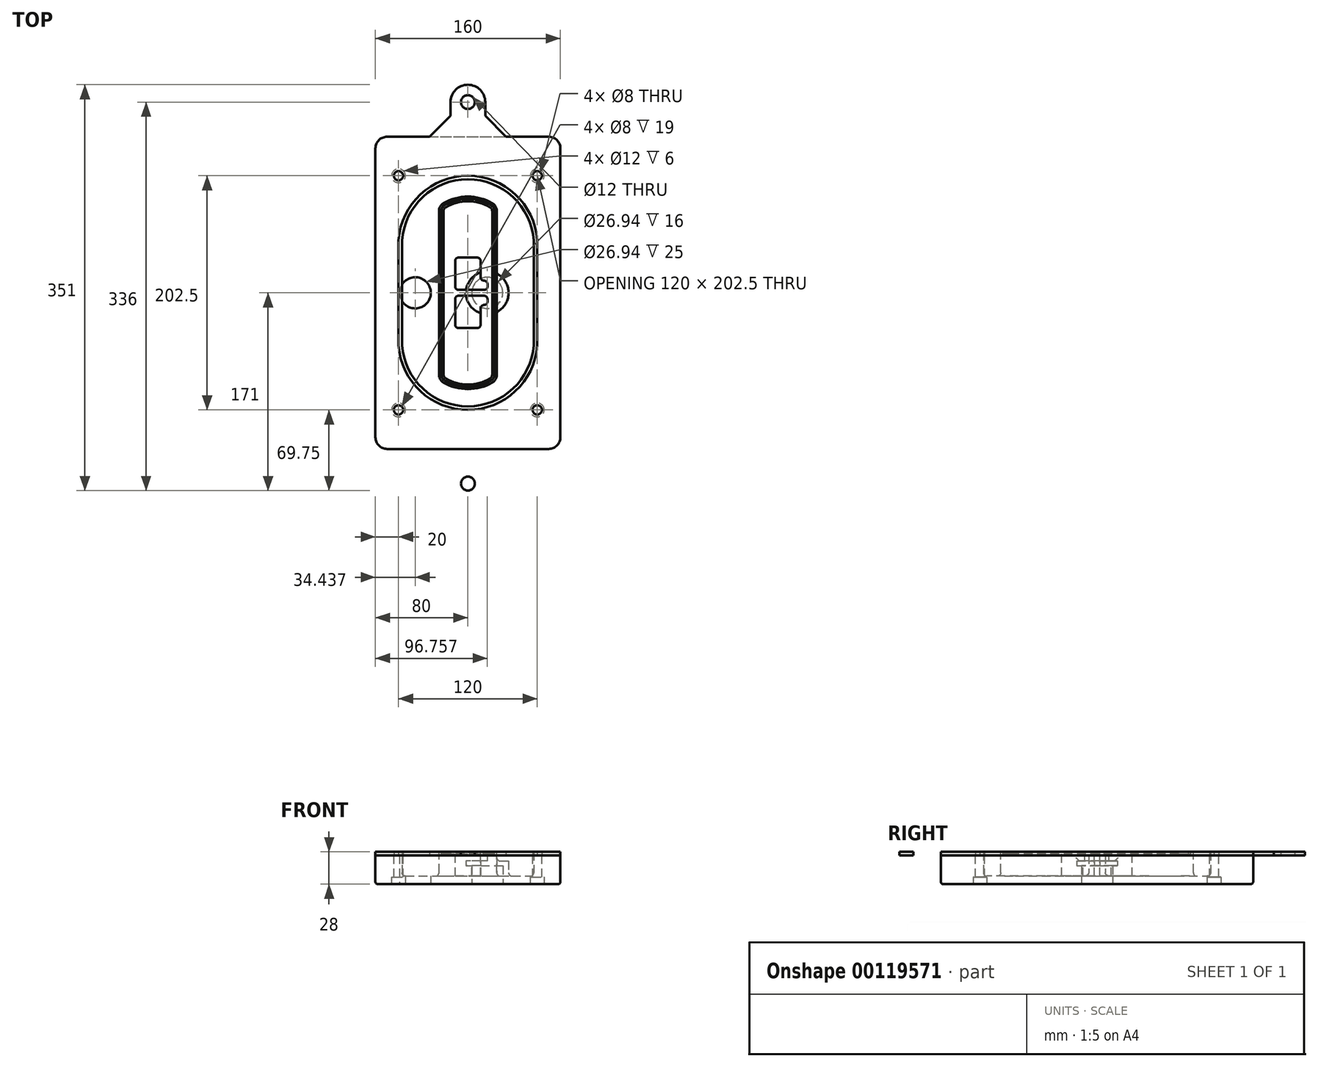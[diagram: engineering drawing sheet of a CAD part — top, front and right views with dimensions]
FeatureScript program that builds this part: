
annotation { "Feature Type Name" : "Feature", "Feature Type Description" : "" }
export const myFeature = defineFeature(function(context is Context, id is Id, definition is map)
    precondition{}
    {
        {
            var Q0;
            Q0=qCreatedBy(makeId("Top.planeOp"),FACE);
            var sketch = newSketch(context, id + "F0", { "sketchPlane" : qUnion([Q0])});
            skPoint(sketch, "E0.rect.middle", {"position": v(0, 0) * mm});
            skLineSegment(sketch, "E1.bottom", {"start": v(-70, -135) * mm, "end": v(70, -135) * mm});
            skLineSegment(sketch, "E1.top", {"start": v(-70, 135) * mm, "end": v(70, 135) * mm});
            skLineSegment(sketch, "E1.left", {"start": v(-80, -125) * mm, "end": v(-80, 125) * mm});
            skLineSegment(sketch, "E1.right", {"start": v(80, -125) * mm, "end": v(80, 125) * mm});
            skLineSegment(sketch, "E2", {"start": v(-80, 135) * mm, "end": v(80, -135) * mm, "construction": true});
            skLineSegment(sketch, "E3", {"start": v(80, 135) * mm, "end": v(-80, -135) * mm, "construction": true});
            skCircle(sketch, "E4", {"center": v(-60, 101.25) * mm, "radius": 4 * mm});
            skCircle(sketch, "E5", {"center": v(60, 101.25) * mm, "radius": 4 * mm});
            skCircle(sketch, "E6", {"center": v(60, -101.25) * mm, "radius": 4 * mm});
            skCircle(sketch, "E7", {"center": v(-60, -101.25) * mm, "radius": 4 * mm});
            skLineSegment(sketch, "E8", {"start": v(-60, 101.25) * mm, "end": v(60, 101.25) * mm, "construction": true});
            skLineSegment(sketch, "E9", {"start": v(60, 101.25) * mm, "end": v(60, -101.25) * mm, "construction": true});
            skLineSegment(sketch, "E10", {"start": v(60, -101.25) * mm, "end": v(-60, -101.25) * mm, "construction": true});
            skLineSegment(sketch, "E11", {"start": v(-60, -101.25) * mm, "end": v(-60, 101.25) * mm, "construction": true});
            skLineSegment(sketch, "E12", {"start": v(-60, 44.66) * mm, "end": v(-60, -44.66) * mm});
            skLineSegment(sketch, "E13", {"start": v(60, 44.66) * mm, "end": v(60, -44.66) * mm});
            skArc(sketch, "E14", {"start": v(59.98, 45.37) * mm, "mid": v(0, 101.25) * mm, "end": v(-59.98, 45.37) * mm});
            skArc(sketch, "E15", {"start": v(-59.98, -45.37) * mm, "mid": v(0, -101.25) * mm, "end": v(59.98, -45.37) * mm});
            skLineSegment(sketch, "E16", {"start": v(-60, 0) * mm, "end": v(60, 0) * mm, "construction": true});
            skPoint(sketch, "E17.visualSharp", {"position": v(-60, -45) * mm});
            skArc(sketch, "E17.filletArc", {"start": v(-60, -44.66) * mm, "mid": v(-60, -45.02) * mm, "end": v(-59.98, -45.37) * mm});
            skPoint(sketch, "E18.visualSharp", {"position": v(-60, 45) * mm});
            skArc(sketch, "E18.filletArc", {"start": v(-59.98, 45.37) * mm, "mid": v(-60, 45.02) * mm, "end": v(-60, 44.66) * mm});
            skPoint(sketch, "E19.visualSharp", {"position": v(60, 45) * mm});
            skArc(sketch, "E19.filletArc", {"start": v(60, 44.66) * mm, "mid": v(60, 45.02) * mm, "end": v(59.98, 45.37) * mm});
            skPoint(sketch, "E20.visualSharp", {"position": v(60, -45) * mm});
            skArc(sketch, "E20.filletArc", {"start": v(59.98, -45.37) * mm, "mid": v(60, -45.02) * mm, "end": v(60, -44.66) * mm});
            skPoint(sketch, "E21.visualSharp", {"position": v(-80, 135) * mm});
            skArc(sketch, "E21.filletArc", {"start": v(-70, 135) * mm, "mid": v(-77.07, 132.07) * mm, "end": v(-80, 125) * mm});
            skPoint(sketch, "E22.visualSharp", {"position": v(80, 135) * mm});
            skArc(sketch, "E22.filletArc", {"start": v(80, 125) * mm, "mid": v(77.07, 132.07) * mm, "end": v(70, 135) * mm});
            skPoint(sketch, "E23.visualSharp", {"position": v(80, -135) * mm});
            skArc(sketch, "E23.filletArc", {"start": v(70, -135) * mm, "mid": v(77.07, -132.07) * mm, "end": v(80, -125) * mm});
            skPoint(sketch, "E24.visualSharp", {"position": v(-80, -135) * mm});
            skArc(sketch, "E24.filletArc", {"start": v(-80, -125) * mm, "mid": v(-77.07, -132.07) * mm, "end": v(-70, -135) * mm});
            skArc(sketch, "E25.0", {"start": v(57, 44.66) * mm, "mid": v(57, 44.9) * mm, "end": v(56.98, 45.16) * mm});
            skLineSegment(sketch, "E25.1", {"start": v(57, 44.66) * mm, "end": v(57, -44.66) * mm});
            skArc(sketch, "E25.2", {"start": v(56.98, -45.16) * mm, "mid": v(57, -44.9) * mm, "end": v(57, -44.66) * mm});
            skArc(sketch, "E25.3", {"start": v(-56.98, -45.16) * mm, "mid": v(0, -98.25) * mm, "end": v(56.98, -45.16) * mm});
            skArc(sketch, "E25.4", {"start": v(-57, -44.66) * mm, "mid": v(-57, -44.9) * mm, "end": v(-56.98, -45.16) * mm});
            skArc(sketch, "E25.5", {"start": v(56.98, 45.16) * mm, "mid": v(0, 98.25) * mm, "end": v(-56.98, 45.16) * mm});
            skLineSegment(sketch, "E25.6", {"start": v(-57, 44.66) * mm, "end": v(-57, -44.66) * mm});
            skArc(sketch, "E25.7", {"start": v(-56.98, 45.16) * mm, "mid": v(-57, 44.9) * mm, "end": v(-57, 44.66) * mm});
            skArc(sketch, "E26.0", {"start": v(-63.97, 45.65) * mm, "mid": v(-64, 45.16) * mm, "end": v(-64, 44.66) * mm});
            skArc(sketch, "E26.1", {"start": v(63.97, 45.65) * mm, "mid": v(0, 105.25) * mm, "end": v(-63.97, 45.65) * mm});
            skArc(sketch, "E26.2", {"start": v(64, 44.66) * mm, "mid": v(64, 45.16) * mm, "end": v(63.97, 45.65) * mm});
            skLineSegment(sketch, "E26.3", {"start": v(64, 44.66) * mm, "end": v(64, -44.66) * mm});
            skArc(sketch, "E26.4", {"start": v(63.97, -45.65) * mm, "mid": v(64, -45.16) * mm, "end": v(64, -44.66) * mm});
            skLineSegment(sketch, "E26.5", {"start": v(-64, 44.66) * mm, "end": v(-64, -44.66) * mm});
            skArc(sketch, "E26.6", {"start": v(-63.97, -45.65) * mm, "mid": v(0, -105.25) * mm, "end": v(63.97, -45.65) * mm});
            skArc(sketch, "E26.7", {"start": v(-64, -44.66) * mm, "mid": v(-64, -45.16) * mm, "end": v(-63.97, -45.65) * mm});
            skSolve(sketch);
        }
        {
            var Q0;
            Q0=makeQuery(id+"F0.imprint","IMPRINT",FACE,{"disambiguationData":[TD([[makeQuery(id+"F0.imprint","IMPRINT",EDGE,{"derivedFrom":sQuery(id+"F0.wireOp",EDGE,"E1.bottom")}),1.0]])]});
            var Q1;
            Q1=makeQuery(id+"F0.imprint","IMPRINT",FACE,{"disambiguationData":[TD([[makeQuery(id+"F0.imprint","IMPRINT",EDGE,{"derivedFrom":sQuery(id+"F0.wireOp",EDGE,"E12")}),1.0]])]});
            var Q2;
            Q2=makeQuery(id+"F0.imprint","IMPRINT",FACE,{"disambiguationData":[TD([[makeQuery(id+"F0.imprint","IMPRINT",EDGE,{"derivedFrom":sQuery(id+"F0.wireOp",EDGE,"E25.0")}),1.0]])]});
            var Q3;
            Q3=makeQuery(id+"F0.imprint","IMPRINT",FACE,{"disambiguationData":[TD([[makeQuery(id+"F0.imprint","IMPRINT",EDGE,{"derivedFrom":sQuery(id+"F0.wireOp",EDGE,"E12")}),-1.0]])]});
            extrude(context, id + "F1", {"entities" : qUnion([Q0, Q1, Q2, Q3]), "oppositeDirection" : true, "depth" : 25 * mm});
        }
        {
            var Q0;
            Q0=makeQuery(id+"F0.imprint","IMPRINT",FACE,{"disambiguationData":[TD([[makeQuery(id+"F0.imprint","IMPRINT",EDGE,{"derivedFrom":sQuery(id+"F0.wireOp",EDGE,"E12")}),1.0]])]});
            extrude(context, id + "F2", {"entities" : qUnion([Q0]), "operationType" : NewBodyOperationType.ADD, "depth" : 3 * mm});
        }
        {
            var Q0;
            Q0=makeQuery(id+"F0.imprint","IMPRINT",FACE,{"disambiguationData":[TD([[makeQuery(id+"F0.imprint","IMPRINT",EDGE,{"derivedFrom":sQuery(id+"F0.wireOp",EDGE,"E25.0")}),1.0]])]});
            extrude(context, id + "F3", {"entities" : qUnion([Q0]), "operationType" : NewBodyOperationType.REMOVE, "oppositeDirection" : true, "depth" : 18 * mm});
        }
        {
            var Q0;
            Q0=makeQuery(id+"F2.opExtrude","CAP_FACE",FACE,{"disambiguationData":[OSD([sQuery(id+"F0.wireOp",EDGE,"E12"),sQuery(id+"F0.wireOp",EDGE,"E13"),sQuery(id+"F0.wireOp",EDGE,"E14"),sQuery(id+"F0.wireOp",EDGE,"E15"),sQuery(id+"F0.wireOp",EDGE,"E17.filletArc"),sQuery(id+"F0.wireOp",EDGE,"E18.filletArc"),sQuery(id+"F0.wireOp",EDGE,"E19.filletArc"),sQuery(id+"F0.wireOp",EDGE,"E20.filletArc"),sQuery(id+"F0.wireOp",EDGE,"E25.0"),sQuery(id+"F0.wireOp",EDGE,"E25.1"),sQuery(id+"F0.wireOp",EDGE,"E25.2"),sQuery(id+"F0.wireOp",EDGE,"E25.3"),sQuery(id+"F0.wireOp",EDGE,"E25.4"),sQuery(id+"F0.wireOp",EDGE,"E25.5"),sQuery(id+"F0.wireOp",EDGE,"E25.6"),sQuery(id+"F0.wireOp",EDGE,"E25.7")])],"isStart":false});
            var sketch = newSketch(context, id + "F4", { "sketchPlane" : qUnion([Q0])});
            skArc(sketch, "E27.0", {"start": v(-20.99, -77.65) * mm, "mid": v(0, -83.25) * mm, "end": v(20.99, -77.65) * mm});
            skArc(sketch, "E28.0", {"start": v(20.99, 77.65) * mm, "mid": v(0, 83.25) * mm, "end": v(-20.99, 77.65) * mm});
            skLineSegment(sketch, "E29", {"start": v(-25, 70.71) * mm, "end": v(-25, -70.71) * mm});
            skLineSegment(sketch, "E30", {"start": v(25, 70.71) * mm, "end": v(25, -70.71) * mm});
            skLineSegment(sketch, "E31", {"start": v(-25, 75.03) * mm, "end": v(25, 75.03) * mm, "construction": true});
            skLineSegment(sketch, "E32", {"start": v(-25, -75.03) * mm, "end": v(25, -75.03) * mm, "construction": true});
            skPoint(sketch, "E33.visualSharp", {"position": v(-25, 75.03) * mm});
            skArc(sketch, "E33.filletArc", {"start": v(-20.99, 77.65) * mm, "mid": v(-23.92, 74.72) * mm, "end": v(-25, 70.71) * mm});
            skPoint(sketch, "E34.visualSharp", {"position": v(25, 75.03) * mm});
            skArc(sketch, "E34.filletArc", {"start": v(25, 70.71) * mm, "mid": v(23.92, 74.72) * mm, "end": v(20.99, 77.65) * mm});
            skPoint(sketch, "E35.visualSharp", {"position": v(25, -75.03) * mm});
            skArc(sketch, "E35.filletArc", {"start": v(20.99, -77.65) * mm, "mid": v(23.92, -74.72) * mm, "end": v(25, -70.71) * mm});
            skPoint(sketch, "E36.visualSharp", {"position": v(-25, -75.03) * mm});
            skArc(sketch, "E36.filletArc", {"start": v(-25, -70.71) * mm, "mid": v(-23.92, -74.72) * mm, "end": v(-20.99, -77.65) * mm});
            skArc(sketch, "E37.0", {"start": v(56.98, 45.16) * mm, "mid": v(0, 98.25) * mm, "end": v(-56.98, 45.16) * mm});
            skArc(sketch, "E37.1", {"start": v(-56.98, 45.16) * mm, "mid": v(-57, 44.9) * mm, "end": v(-57, 44.66) * mm});
            skLineSegment(sketch, "E37.2", {"start": v(-57, 44.66) * mm, "end": v(-57, -44.66) * mm});
            skArc(sketch, "E37.3", {"start": v(-57, -44.66) * mm, "mid": v(-57, -44.9) * mm, "end": v(-56.98, -45.16) * mm});
            skArc(sketch, "E37.4", {"start": v(-56.98, -45.16) * mm, "mid": v(0, -98.25) * mm, "end": v(56.98, -45.16) * mm});
            skArc(sketch, "E37.5", {"start": v(56.98, -45.16) * mm, "mid": v(57, -44.9) * mm, "end": v(57, -44.66) * mm});
            skLineSegment(sketch, "E37.6", {"start": v(57, 44.66) * mm, "end": v(57, -44.66) * mm});
            skArc(sketch, "E37.7", {"start": v(57, 44.66) * mm, "mid": v(57, 44.9) * mm, "end": v(56.98, 45.16) * mm});
            skLineSegment(sketch, "E38.0", {"start": v(23, 70.71) * mm, "end": v(23, -70.71) * mm});
            skArc(sketch, "E38.1", {"start": v(19.99, -75.92) * mm, "mid": v(22.2, -73.72) * mm, "end": v(23, -70.71) * mm});
            skArc(sketch, "E38.2", {"start": v(-19.99, -75.92) * mm, "mid": v(0, -81.25) * mm, "end": v(19.99, -75.92) * mm});
            skArc(sketch, "E38.3", {"start": v(-23, -70.71) * mm, "mid": v(-22.2, -73.72) * mm, "end": v(-19.99, -75.92) * mm});
            skLineSegment(sketch, "E38.4", {"start": v(-23, 70.71) * mm, "end": v(-23, -70.71) * mm});
            skArc(sketch, "E38.5", {"start": v(23, 70.71) * mm, "mid": v(22.2, 73.72) * mm, "end": v(19.99, 75.92) * mm});
            skArc(sketch, "E38.6", {"start": v(-19.99, 75.92) * mm, "mid": v(-22.2, 73.72) * mm, "end": v(-23, 70.71) * mm});
            skArc(sketch, "E38.7", {"start": v(19.99, 75.92) * mm, "mid": v(0, 81.25) * mm, "end": v(-19.99, 75.92) * mm});
            skArc(sketch, "E39.0", {"start": v(21, 70.71) * mm, "mid": v(20.46, 72.72) * mm, "end": v(19, 74.18) * mm});
            skLineSegment(sketch, "E39.1", {"start": v(21, 70.71) * mm, "end": v(21, -70.71) * mm});
            skArc(sketch, "E39.2", {"start": v(19, -74.18) * mm, "mid": v(20.46, -72.72) * mm, "end": v(21, -70.71) * mm});
            skArc(sketch, "E39.3", {"start": v(-19, -74.18) * mm, "mid": v(0, -79.25) * mm, "end": v(19, -74.18) * mm});
            skArc(sketch, "E39.4", {"start": v(-21, -70.71) * mm, "mid": v(-20.46, -72.72) * mm, "end": v(-19, -74.18) * mm});
            skArc(sketch, "E39.5", {"start": v(19, 74.18) * mm, "mid": v(0, 79.25) * mm, "end": v(-19, 74.18) * mm});
            skLineSegment(sketch, "E39.6", {"start": v(-21, 70.71) * mm, "end": v(-21, -70.71) * mm});
            skArc(sketch, "E39.7", {"start": v(-19, 74.18) * mm, "mid": v(-20.46, 72.72) * mm, "end": v(-21, 70.71) * mm});
            skLineSegment(sketch, "E40", {"start": v(-25, 0) * mm, "end": v(25, 0) * mm, "construction": true});
            skLineSegment(sketch, "E41", {"start": v(-11, 5.5) * mm, "end": v(-11, 27.5) * mm});
            skLineSegment(sketch, "E42", {"start": v(-8, 30.5) * mm, "end": v(8, 30.5) * mm});
            skLineSegment(sketch, "E43", {"start": v(11, 27.5) * mm, "end": v(11, 13.5) * mm});
            skLineSegment(sketch, "E44", {"start": v(14, 10.5) * mm, "end": v(14, 10.5) * mm});
            skLineSegment(sketch, "E45", {"start": v(17, 7.5) * mm, "end": v(17, 5.5) * mm});
            skLineSegment(sketch, "E46", {"start": v(14, 2.5) * mm, "end": v(-8, 2.5) * mm});
            skPoint(sketch, "E47.visualSharp", {"position": v(-11, 30.5) * mm});
            skArc(sketch, "E47.filletArc", {"start": v(-8, 30.5) * mm, "mid": v(-10.12, 29.62) * mm, "end": v(-11, 27.5) * mm});
            skPoint(sketch, "E48.visualSharp", {"position": v(11, 30.5) * mm});
            skArc(sketch, "E48.filletArc", {"start": v(11, 27.5) * mm, "mid": v(10.12, 29.62) * mm, "end": v(8, 30.5) * mm});
            skPoint(sketch, "E49.visualSharp", {"position": v(11, 10.5) * mm});
            skArc(sketch, "E49.filletArc", {"start": v(11, 13.5) * mm, "mid": v(11.88, 11.38) * mm, "end": v(14, 10.5) * mm});
            skPoint(sketch, "E50.visualSharp", {"position": v(17, 10.5) * mm});
            skArc(sketch, "E50.filletArc", {"start": v(17, 7.5) * mm, "mid": v(16.12, 9.62) * mm, "end": v(14, 10.5) * mm});
            skPoint(sketch, "E51.visualSharp", {"position": v(17, 2.5) * mm});
            skArc(sketch, "E51.filletArc", {"start": v(14, 2.5) * mm, "mid": v(16.12, 3.38) * mm, "end": v(17, 5.5) * mm});
            skPoint(sketch, "E52.visualSharp", {"position": v(-11, 2.5) * mm});
            skArc(sketch, "E52.filletArc", {"start": v(-11, 5.5) * mm, "mid": v(-10.12, 3.38) * mm, "end": v(-8, 2.5) * mm});
            skLineSegment(sketch, "E53.0.MirrorCS", {"start": v(14, -2.5) * mm, "end": v(-8, -2.5) * mm});
            skArc(sketch, "E54.0.MirrorCS", {"start": v(-11, -5.5) * mm, "mid": v(-10.12, -3.38) * mm, "end": v(-8, -2.5) * mm});
            skLineSegment(sketch, "E55.0.MirrorCS", {"start": v(-11, -5.5) * mm, "end": v(-11, -27.5) * mm});
            skArc(sketch, "E56.0.MirrorCS", {"start": v(-8, -30.5) * mm, "mid": v(-10.12, -29.62) * mm, "end": v(-11, -27.5) * mm});
            skLineSegment(sketch, "E57.0.MirrorCS", {"start": v(-8, -30.5) * mm, "end": v(8, -30.5) * mm});
            skArc(sketch, "E58.0.MirrorCS", {"start": v(11, -27.5) * mm, "mid": v(10.12, -29.62) * mm, "end": v(8, -30.5) * mm});
            skLineSegment(sketch, "E59.0.MirrorCS", {"start": v(11, -27.5) * mm, "end": v(11, -13.5) * mm});
            skArc(sketch, "E60.0.MirrorCS", {"start": v(11, -13.5) * mm, "mid": v(11.88, -11.38) * mm, "end": v(14, -10.5) * mm});
            skArc(sketch, "E61.0.MirrorCS", {"start": v(17, -7.5) * mm, "mid": v(16.12, -9.62) * mm, "end": v(14, -10.5) * mm});
            skLineSegment(sketch, "E62.0.MirrorCS", {"start": v(17, -7.5) * mm, "end": v(17, -5.5) * mm});
            skArc(sketch, "E63.0.MirrorCS", {"start": v(14, -2.5) * mm, "mid": v(16.12, -3.38) * mm, "end": v(17, -5.5) * mm});
            skSolve(sketch);
        }
        {
            var Q0;
            Q0=makeQuery(id+"F4.imprint","IMPRINT",FACE,{"disambiguationData":[TD([[makeQuery(id+"F4.imprint","IMPRINT",EDGE,{"derivedFrom":sQuery(id+"F4.wireOp",EDGE,"E27.0")}),1.0]])]});
            var Q1;
            Q1=makeQuery(id+"F4.imprint","IMPRINT",FACE,{"disambiguationData":[TD([[makeQuery(id+"F4.imprint","IMPRINT",EDGE,{"derivedFrom":sQuery(id+"F4.wireOp",EDGE,"E38.0")}),-1.0]])]});
            var Q2;
            Q2=makeQuery(id+"F4.imprint","IMPRINT",FACE,{"disambiguationData":[TD([[makeQuery(id+"F4.imprint","IMPRINT",EDGE,{"derivedFrom":sQuery(id+"F4.wireOp",EDGE,"E39.0")}),1.0]])]});
            extrude(context, id + "F5", {"entities" : qUnion([Q0, Q1, Q2]), "operationType" : NewBodyOperationType.ADD, "endBound" : BoundingType.UP_TO_NEXT, "oppositeDirection" : true, "depth" : 25 * mm});
        }
        {
            var Q0;
            Q0=makeQuery(id+"F4.imprint","IMPRINT",FACE,{"disambiguationData":[TD([[makeQuery(id+"F4.imprint","IMPRINT",EDGE,{"derivedFrom":sQuery(id+"F4.wireOp",EDGE,"E38.0")}),-1.0]])]});
            extrude(context, id + "F6", {"entities" : qUnion([Q0]), "operationType" : NewBodyOperationType.REMOVE, "oppositeDirection" : true, "depth" : 2 * mm});
        }
        {
            var Q0;
            Q0=makeQuery(id+"F1.opExtrude","CAP_FACE",FACE,{"disambiguationData":[OSD([sQuery(id+"F0.wireOp",EDGE,"E1.bottom"),sQuery(id+"F0.wireOp",EDGE,"E1.top"),sQuery(id+"F0.wireOp",EDGE,"E1.left"),sQuery(id+"F0.wireOp",EDGE,"E1.right"),sQuery(id+"F0.wireOp",EDGE,"E4"),sQuery(id+"F0.wireOp",EDGE,"E5"),sQuery(id+"F0.wireOp",EDGE,"E6"),sQuery(id+"F0.wireOp",EDGE,"E7"),sQuery(id+"F0.wireOp",EDGE,"E21.filletArc"),sQuery(id+"F0.wireOp",EDGE,"E22.filletArc"),sQuery(id+"F0.wireOp",EDGE,"E23.filletArc"),sQuery(id+"F0.wireOp",EDGE,"E24.filletArc")])],"isStart":false});
            var sketch = newSketch(context, id + "F7", { "sketchPlane" : qUnion([Q0])});
            skCircle(sketch, "E64", {"center": v(16.76, 0) * mm, "radius": 13.47 * mm});
            skCircle(sketch, "E65", {"center": v(-45.56, 0) * mm, "radius": 13.47 * mm});
            skLineSegment(sketch, "E66", {"start": v(80, 0) * mm, "end": v(-80, 0) * mm});
            skCircle(sketch, "E67", {"center": v(16.76, 0) * mm, "radius": 18.47 * mm});
            skCircle(sketch, "E68", {"center": v(60, -101.25) * mm, "radius": 6 * mm});
            skCircle(sketch, "E69", {"center": v(-60, -101.25) * mm, "radius": 6 * mm});
            skCircle(sketch, "E70", {"center": v(-60, 101.25) * mm, "radius": 6 * mm});
            skCircle(sketch, "E71", {"center": v(60, 101.25) * mm, "radius": 6 * mm});
            skSolve(sketch);
        }
        {
            var Q0;
            {var subQ1=sQuery(id+"F7.wireOp",EDGE,"E66");var subQ4=sQuery(id+"F7.wireOp",EDGE,"E64");var subQ6=makeQuery(id+"F7.imprint","INTERSECT",VERTEX,{"disambiguationData":[OD(0.0)],"derivedFrom":[subQ4,subQ1]});Q0=makeQuery(id+"F7.imprint","IMPRINT",FACE,{"disambiguationData":[TD([[makeQuery(id+"F7.imprint","IMPRINT",EDGE,{"disambiguationData":[TD([[subQ6,-1.0]])],"derivedFrom":subQ4}),-1.0]])]});}
            var Q1;
            {var subQ0=sQuery(id+"F7.wireOp",EDGE,"E66");var subQ1=sQuery(id+"F7.wireOp",EDGE,"E64");var subQ3=makeQuery(id+"F7.imprint","INTERSECT",VERTEX,{"disambiguationData":[OD(0.0)],"derivedFrom":[subQ1,subQ0]});Q1=makeQuery(id+"F7.imprint","IMPRINT",FACE,{"disambiguationData":[TD([[makeQuery(id+"F7.imprint","IMPRINT",EDGE,{"disambiguationData":[TD([[subQ3,-1.0]])],"derivedFrom":subQ1}),1.0]])]});}
            var Q2;
            {var subQ0=sQuery(id+"F7.wireOp",EDGE,"E66");var subQ1=sQuery(id+"F7.wireOp",EDGE,"E64");var subQ3=makeQuery(id+"F7.imprint","INTERSECT",VERTEX,{"disambiguationData":[OD(0.0)],"derivedFrom":[subQ1,subQ0]});Q2=makeQuery(id+"F7.imprint","IMPRINT",FACE,{"disambiguationData":[TD([[makeQuery(id+"F7.imprint","IMPRINT",EDGE,{"disambiguationData":[TD([[subQ3,1.0]])],"derivedFrom":subQ1}),1.0]])]});}
            var Q3;
            {var subQ1=sQuery(id+"F7.wireOp",EDGE,"E66");var subQ4=sQuery(id+"F7.wireOp",EDGE,"E64");var subQ6=makeQuery(id+"F7.imprint","INTERSECT",VERTEX,{"disambiguationData":[OD(0.0)],"derivedFrom":[subQ4,subQ1]});Q3=makeQuery(id+"F7.imprint","IMPRINT",FACE,{"disambiguationData":[TD([[makeQuery(id+"F7.imprint","IMPRINT",EDGE,{"disambiguationData":[TD([[subQ6,1.0]])],"derivedFrom":subQ4}),-1.0]])]});}
            extrude(context, id + "F8", {"entities" : qUnion([Q0, Q1, Q2, Q3]), "operationType" : NewBodyOperationType.ADD, "oppositeDirection" : true, "depth" : 20 * mm});
        }
        {
            var Q0;
            {var subQ0=sQuery(id+"F7.wireOp",EDGE,"E66");var subQ1=sQuery(id+"F7.wireOp",EDGE,"E64");var subQ3=makeQuery(id+"F7.imprint","INTERSECT",VERTEX,{"disambiguationData":[OD(0.0)],"derivedFrom":[subQ1,subQ0]});Q0=makeQuery(id+"F7.imprint","IMPRINT",FACE,{"disambiguationData":[TD([[makeQuery(id+"F7.imprint","IMPRINT",EDGE,{"disambiguationData":[TD([[subQ3,-1.0]])],"derivedFrom":subQ1}),1.0]])]});}
            var Q1;
            {var subQ0=sQuery(id+"F7.wireOp",EDGE,"E66");var subQ1=sQuery(id+"F7.wireOp",EDGE,"E64");var subQ3=makeQuery(id+"F7.imprint","INTERSECT",VERTEX,{"disambiguationData":[OD(0.0)],"derivedFrom":[subQ1,subQ0]});Q1=makeQuery(id+"F7.imprint","IMPRINT",FACE,{"disambiguationData":[TD([[makeQuery(id+"F7.imprint","IMPRINT",EDGE,{"disambiguationData":[TD([[subQ3,1.0]])],"derivedFrom":subQ1}),1.0]])]});}
            extrude(context, id + "F9", {"entities" : qUnion([Q0, Q1]), "operationType" : NewBodyOperationType.REMOVE, "oppositeDirection" : true, "depth" : 16 * mm});
        }
        {
            var Q0;
            {var subQ0=sQuery(id+"F7.wireOp",EDGE,"E66");var subQ1=sQuery(id+"F7.wireOp",EDGE,"E65");var subQ3=makeQuery(id+"F7.imprint","INTERSECT",VERTEX,{"disambiguationData":[OD(0.0)],"derivedFrom":[subQ1,subQ0]});Q0=makeQuery(id+"F7.imprint","IMPRINT",FACE,{"disambiguationData":[TD([[makeQuery(id+"F7.imprint","IMPRINT",EDGE,{"disambiguationData":[TD([[subQ3,-1.0]])],"derivedFrom":subQ1}),1.0]])]});}
            var Q1;
            {var subQ0=sQuery(id+"F7.wireOp",EDGE,"E66");var subQ1=sQuery(id+"F7.wireOp",EDGE,"E65");var subQ3=makeQuery(id+"F7.imprint","INTERSECT",VERTEX,{"disambiguationData":[OD(0.0)],"derivedFrom":[subQ1,subQ0]});Q1=makeQuery(id+"F7.imprint","IMPRINT",FACE,{"disambiguationData":[TD([[makeQuery(id+"F7.imprint","IMPRINT",EDGE,{"disambiguationData":[TD([[subQ3,1.0]])],"derivedFrom":subQ1}),1.0]])]});}
            extrude(context, id + "F10", {"entities" : qUnion([Q0, Q1]), "operationType" : NewBodyOperationType.REMOVE, "oppositeDirection" : true, "depth" : 25 * mm});
        }
        {
            var Q0;
            Q0=makeQuery(id+"F7.imprint","IMPRINT",FACE,{"disambiguationData":[TD([[makeQuery(id+"F7.imprint","IMPRINT",EDGE,{"derivedFrom":sQuery(id+"F7.wireOp",EDGE,"E68")}),1.0]])]});
            var Q1;
            Q1=makeQuery(id+"F7.imprint","IMPRINT",FACE,{"disambiguationData":[TD([[makeQuery(id+"F7.imprint","IMPRINT",EDGE,{"derivedFrom":makeQuery(id+"F1.opExtrude","CAP_EDGE",EDGE,{"disambiguationData":[OSD([sQuery(id+"F0.wireOp",EDGE,"E5")])],"isStart":false})}),-1.0]])]});
            var Q2;
            Q2=makeQuery(id+"F7.imprint","IMPRINT",FACE,{"disambiguationData":[TD([[makeQuery(id+"F7.imprint","IMPRINT",EDGE,{"derivedFrom":sQuery(id+"F7.wireOp",EDGE,"E69")}),1.0]])]});
            var Q3;
            Q3=makeQuery(id+"F7.imprint","IMPRINT",FACE,{"disambiguationData":[TD([[makeQuery(id+"F7.imprint","IMPRINT",EDGE,{"derivedFrom":makeQuery(id+"F1.opExtrude","CAP_EDGE",EDGE,{"disambiguationData":[OSD([sQuery(id+"F0.wireOp",EDGE,"E4")])],"isStart":false})}),-1.0]])]});
            var Q4;
            Q4=makeQuery(id+"F7.imprint","IMPRINT",FACE,{"disambiguationData":[TD([[makeQuery(id+"F7.imprint","IMPRINT",EDGE,{"derivedFrom":sQuery(id+"F7.wireOp",EDGE,"E70")}),1.0]])]});
            var Q5;
            Q5=makeQuery(id+"F7.imprint","IMPRINT",FACE,{"disambiguationData":[TD([[makeQuery(id+"F7.imprint","IMPRINT",EDGE,{"derivedFrom":makeQuery(id+"F1.opExtrude","CAP_EDGE",EDGE,{"disambiguationData":[OSD([sQuery(id+"F0.wireOp",EDGE,"E7")])],"isStart":false})}),-1.0]])]});
            var Q6;
            Q6=makeQuery(id+"F7.imprint","IMPRINT",FACE,{"disambiguationData":[TD([[makeQuery(id+"F7.imprint","IMPRINT",EDGE,{"derivedFrom":sQuery(id+"F7.wireOp",EDGE,"E71")}),1.0]])]});
            var Q7;
            Q7=makeQuery(id+"F7.imprint","IMPRINT",FACE,{"disambiguationData":[TD([[makeQuery(id+"F7.imprint","IMPRINT",EDGE,{"derivedFrom":makeQuery(id+"F1.opExtrude","CAP_EDGE",EDGE,{"disambiguationData":[OSD([sQuery(id+"F0.wireOp",EDGE,"E6")])],"isStart":false})}),-1.0]])]});
            extrude(context, id + "F11", {"entities" : qUnion([Q0, Q1, Q2, Q3, Q4, Q5, Q6, Q7]), "operationType" : NewBodyOperationType.REMOVE, "oppositeDirection" : true, "depth" : 6 * mm});
        }
        {
            var Q0;
            Q0=makeQuery(id+"F9.boolean.opBoolean","COPY",FACE,{"derivedFrom":makeQuery(id+"F9.opExtrude","CAP_FACE",FACE,{"disambiguationData":[OSD([sQuery(id+"F7.wireOp",EDGE,"E64")])],"isStart":false})});
            var sketch = newSketch(context, id + "F12", { "sketchPlane" : qUnion([Q0])});
            skArc(sketch, "E72.0", {"start": v(11, 17.55) * mm, "mid": v(2.57, 11.82) * mm, "end": v(-1.54, 2.5) * mm});
            skArc(sketch, "E72.1", {"start": v(-1.54, -2.5) * mm, "mid": v(2.57, -11.82) * mm, "end": v(11, -17.55) * mm});
            skLineSegment(sketch, "E73", {"start": v(-1.54, -2.5) * mm, "end": v(14, -2.5) * mm});
            skLineSegment(sketch, "E74.0", {"start": v(14, 2.5) * mm, "end": v(-1.54, 2.5) * mm});
            skArc(sketch, "E74.1", {"start": v(14, 2.5) * mm, "mid": v(16.12, 3.38) * mm, "end": v(17, 5.5) * mm});
            skLineSegment(sketch, "E74.2", {"start": v(17, 7.5) * mm, "end": v(17, 5.5) * mm});
            skArc(sketch, "E74.3", {"start": v(17, 7.5) * mm, "mid": v(16.12, 9.62) * mm, "end": v(14, 10.5) * mm});
            skArc(sketch, "E74.4", {"start": v(11, 13.5) * mm, "mid": v(11.88, 11.38) * mm, "end": v(14, 10.5) * mm});
            skLineSegment(sketch, "E74.5", {"start": v(11, 17.55) * mm, "end": v(11, 13.5) * mm});
            skLineSegment(sketch, "E74.7", {"start": v(14, -2.5) * mm, "end": v(-1.54, -2.5) * mm});
            skArc(sketch, "E74.8", {"start": v(14, -2.5) * mm, "mid": v(16.12, -3.38) * mm, "end": v(17, -5.5) * mm});
            skLineSegment(sketch, "E74.9", {"start": v(17, -7.5) * mm, "end": v(17, -5.5) * mm});
            skArc(sketch, "E74.10", {"start": v(17, -7.5) * mm, "mid": v(16.12, -9.62) * mm, "end": v(14, -10.5) * mm});
            skArc(sketch, "E74.11", {"start": v(11, -13.5) * mm, "mid": v(11.88, -11.38) * mm, "end": v(14, -10.5) * mm});
            skLineSegment(sketch, "E74.12", {"start": v(11, -17.55) * mm, "end": v(11, -13.5) * mm});
            skPoint(sketch, "E75.orphan", {"position": v(11, -27.5) * mm});
            skPoint(sketch, "E76.orphan", {"position": v(-8, -2.5) * mm});
            skPoint(sketch, "E77.orphan", {"position": v(-8, 2.5) * mm});
            skPoint(sketch, "E78.orphan", {"position": v(11, 27.5) * mm});
            skSolve(sketch);
        }
        {
            var Q0;
            {var subQ7=sQuery(id+"F12.wireOp",EDGE,"E72.0");var subQ14=sQuery(id+"F12.wireOp",EDGE,"E72.1");var subQ16=sQuery(id+"F12.wireOp",EDGE,"E74.1");var subQ18=sQuery(id+"F12.wireOp",EDGE,"E74.8");Q0=qUnion([makeQuery(id+"F12.imprint","IMPRINT",FACE,{"disambiguationData":[TD([[makeQuery(id+"F12.imprint","IMPRINT",EDGE,{"derivedFrom":subQ7}),1.0]])]}),makeQuery(id+"F12.imprint","IMPRINT",FACE,{"disambiguationData":[TD([[makeQuery(id+"F12.imprint","IMPRINT",EDGE,{"derivedFrom":subQ14}),1.0]])]}),makeQuery(id+"F12.imprint","IMPRINT",FACE,{"disambiguationData":[TD([[makeQuery(id+"F12.imprint","IMPRINT",EDGE,{"derivedFrom":subQ16}),1.0]])]}),makeQuery(id+"F12.imprint","IMPRINT",FACE,{"disambiguationData":[TD([[makeQuery(id+"F12.imprint","IMPRINT",EDGE,{"derivedFrom":subQ18}),-1.0]])]})]);}
            var Q1;
            Q1=makeQuery(id+"F5.boolean.opBoolean","SPLIT",FACE,{"disambiguationData":[TD([makeQuery(id+"F5.opExtrude","SWEPT_FACE",FACE,{"disambiguationData":[OSD([sQuery(id+"F4.wireOp",EDGE,"E41")])]})])],"derivedFrom":makeQuery(id+"F3.boolean.opBoolean","COPY",FACE,{"derivedFrom":makeQuery(id+"F3.opExtrude","CAP_FACE",FACE,{"disambiguationData":[OSD([sQuery(id+"F0.wireOp",EDGE,"E25.0"),sQuery(id+"F0.wireOp",EDGE,"E25.1"),sQuery(id+"F0.wireOp",EDGE,"E25.2"),sQuery(id+"F0.wireOp",EDGE,"E25.3"),sQuery(id+"F0.wireOp",EDGE,"E25.4"),sQuery(id+"F0.wireOp",EDGE,"E25.5"),sQuery(id+"F0.wireOp",EDGE,"E25.6"),sQuery(id+"F0.wireOp",EDGE,"E25.7")])],"isStart":false})})});
            extrude(context, id + "F13", {"entities" : qUnion([Q0]), "operationType" : NewBodyOperationType.REMOVE, "endBound" : BoundingType.UP_TO_SURFACE, "endBoundEntityFace" : qUnion([Q1]), "depth" : 25 * mm});
        }
        {
            var Q0;
            Q0=makeQuery(id+"F3.boolean.opBoolean","COPY",EDGE,{"derivedFrom":makeQuery(id+"F3.opExtrude","CAP_EDGE",EDGE,{"disambiguationData":[OSD([sQuery(id+"F0.wireOp",EDGE,"E25.6")])],"isStart":false})});
            var Q1;
            Q1=makeQuery(id+"F8.boolean.opBoolean","INTERSECT",EDGE,{"derivedFrom":[makeQuery(id+"F5.opExtrude","SWEPT_FACE",FACE,{"disambiguationData":[OSD([sQuery(id+"F4.wireOp",EDGE,"E30")])]}),makeQuery(id+"F8.opExtrude","CAP_FACE",FACE,{"disambiguationData":[OSD([sQuery(id+"F7.wireOp",EDGE,"E67")])],"isStart":false})]});
            var Q2;
            Q2=makeQuery(id+"F8.boolean.opBoolean","INTERSECT",EDGE,{"disambiguationData":[OD(1.0)],"derivedFrom":[makeQuery(id+"F5.opExtrude","SWEPT_FACE",FACE,{"disambiguationData":[OSD([sQuery(id+"F4.wireOp",EDGE,"E30")])]}),makeQuery(id+"F8.opExtrude","SWEPT_FACE",FACE,{"disambiguationData":[OSD([sQuery(id+"F7.wireOp",EDGE,"E67")])]})]});
            var Q3;
            {var subQ0=sQuery(id+"F4.wireOp",EDGE,"E30");Q3=makeQuery(id+"F8.boolean.opBoolean","SPLIT",EDGE,{"disambiguationData":[TD([makeQuery(id+"F5.opExtrude","SWEPT_FACE",FACE,{"disambiguationData":[OSD([sQuery(id+"F4.wireOp",EDGE,"E35.filletArc")])]})])],"derivedFrom":makeQuery(id+"F5.opExtrude","CAP_EDGE",EDGE,{"disambiguationData":[OSD([subQ0])],"isStart":false})});}
            var Q4;
            {var subQ0=sQuery(id+"F0.wireOp",EDGE,"E25.7");var subQ1=sQuery(id+"F0.wireOp",EDGE,"E25.1");var subQ2=sQuery(id+"F0.wireOp",EDGE,"E25.6");var subQ3=sQuery(id+"F0.wireOp",EDGE,"E25.5");var subQ4=sQuery(id+"F0.wireOp",EDGE,"E25.4");var subQ5=sQuery(id+"F0.wireOp",EDGE,"E25.0");var subQ6=sQuery(id+"F0.wireOp",EDGE,"E25.2");var subQ7=sQuery(id+"F0.wireOp",EDGE,"E25.3");Q4=makeQuery(id+"F8.boolean.opBoolean","INTERSECT",EDGE,{"derivedFrom":[makeQuery(id+"F5.boolean.opBoolean","SPLIT",FACE,{"disambiguationData":[TD([makeQuery(id+"F2.opExtrude","SWEPT_FACE",FACE,{"disambiguationData":[OSD([subQ5])]})])],"derivedFrom":makeQuery(id+"F3.boolean.opBoolean","COPY",FACE,{"derivedFrom":makeQuery(id+"F3.opExtrude","CAP_FACE",FACE,{"disambiguationData":[OSD([subQ5,subQ1,subQ6,subQ7,subQ4,subQ3,subQ2,subQ0])],"isStart":false})})}),makeQuery(id+"F8.opExtrude","SWEPT_FACE",FACE,{"disambiguationData":[OSD([sQuery(id+"F7.wireOp",EDGE,"E67")])]})]});}
            var Q5;
            Q5=makeQuery(id+"F8.boolean.opBoolean","INTERSECT",EDGE,{"disambiguationData":[OD(0.0)],"derivedFrom":[makeQuery(id+"F5.opExtrude","SWEPT_FACE",FACE,{"disambiguationData":[OSD([sQuery(id+"F4.wireOp",EDGE,"E30")])]}),makeQuery(id+"F8.opExtrude","SWEPT_FACE",FACE,{"disambiguationData":[OSD([sQuery(id+"F7.wireOp",EDGE,"E67")])]})]});
            fillet(context, id + "F14", {"entities" : qUnion([Q0, Q1, Q2, Q3, Q4, Q5]), "radius" : 3 * mm, "tangentPropagation" : true, "allowEdgeOverflow" : false});
        }
        {
            var Q0;
            Q0=makeQuery(id+"F1.opExtrude","CAP_EDGE",EDGE,{"disambiguationData":[OSD([sQuery(id+"F0.wireOp",EDGE,"E1.bottom")])],"isStart":false});
            fillet(context, id + "F15", {"entities" : qUnion([Q0]), "radius" : 2 * mm, "tangentPropagation" : true, "allowEdgeOverflow" : false});
        }
        {
            var Q0;
            Q0=qCreatedBy(makeId("Top.planeOp"),FACE);
            var sketch = newSketch(context, id + "F16", { "sketchPlane" : qUnion([Q0])});
            skArc(sketch, "E79.0.0", {"start": v(-80, -125) * mm, "mid": v(-77.07, -132.07) * mm, "end": v(-70, -135) * mm});
            skLineSegment(sketch, "E79.0.1", {"start": v(-70, -135) * mm, "end": v(70, -135) * mm});
            skArc(sketch, "E79.0.2", {"start": v(70, -135) * mm, "mid": v(77.07, -132.07) * mm, "end": v(80, -125) * mm});
            skLineSegment(sketch, "E79.0.3", {"start": v(80, -125) * mm, "end": v(80, 125) * mm});
            skArc(sketch, "E79.0.4", {"start": v(80, 125) * mm, "mid": v(77.07, 132.07) * mm, "end": v(70, 135) * mm});
            skLineSegment(sketch, "E79.0.5", {"start": v(70, 135) * mm, "end": v(-70, 135) * mm});
            skArc(sketch, "E79.0.6", {"start": v(-70, 135) * mm, "mid": v(-77.07, 132.07) * mm, "end": v(-80, 125) * mm});
            skLineSegment(sketch, "E79.0.7", {"start": v(-80, 125) * mm, "end": v(-80, -125) * mm});
            skLineSegment(sketch, "E80", {"start": v(0, 135) * mm, "end": v(0, 165) * mm, "construction": true});
            skPoint(sketch, "E80.endSnap0", {"position": v(0, 135) * mm});
            skCircle(sketch, "E81", {"center": v(0, 165) * mm, "radius": 6 * mm});
            skArc(sketch, "E82", {"start": v(15, 165) * mm, "mid": v(0, 180) * mm, "end": v(-15, 165) * mm});
            skLineSegment(sketch, "E83", {"start": v(-15, 165) * mm, "end": v(-15, 153) * mm});
            skLineSegment(sketch, "E84", {"start": v(-15, 153) * mm, "end": v(-33, 135) * mm});
            skLineSegment(sketch, "E85", {"start": v(15, 165) * mm, "end": v(15, 153) * mm});
            skLineSegment(sketch, "E86", {"start": v(15, 153) * mm, "end": v(33, 135) * mm});
            skLineSegment(sketch, "E87", {"start": v(-80, 0) * mm, "end": v(80, 0) * mm, "construction": true});
            skCircle(sketch, "E88.MirrorC", {"center": v(0, -165) * mm, "radius": 6 * mm});
            skArc(sketch, "E89.MirrorCS", {"start": v(15, -165) * mm, "mid": v(0, -180) * mm, "end": v(-15, -165) * mm});
            skLineSegment(sketch, "E90.MirrorCS", {"start": v(-15, -165) * mm, "end": v(-15, -153) * mm});
            skLineSegment(sketch, "E91.MirrorCS", {"start": v(15, -165) * mm, "end": v(15, -153) * mm});
            skLineSegment(sketch, "E92.MirrorCS", {"start": v(15, -153) * mm, "end": v(33, -135) * mm});
            skLineSegment(sketch, "E93.MirrorCS", {"start": v(-15, -153) * mm, "end": v(-33, -135) * mm});
            skLineSegment(sketch, "E94.MirrorCS", {"start": v(0, -135) * mm, "end": v(0, -165) * mm, "construction": true});
            skCircle(sketch, "E95.0", {"center": v(-60, -101.25) * mm, "radius": 4 * mm});
            skCircle(sketch, "E96.0", {"center": v(60, -101.25) * mm, "radius": 4 * mm});
            skCircle(sketch, "E96.1", {"center": v(60, 101.25) * mm, "radius": 4 * mm});
            skCircle(sketch, "E96.2", {"center": v(-60, 101.25) * mm, "radius": 4 * mm});
            skArc(sketch, "E96.3", {"start": v(-59.98, -45.37) * mm, "mid": v(0, -101.25) * mm, "end": v(59.98, -45.37) * mm});
            skLineSegment(sketch, "E96.4", {"start": v(60, 44.66) * mm, "end": v(60, -44.66) * mm});
            skArc(sketch, "E96.5", {"start": v(59.98, 45.37) * mm, "mid": v(0, 101.25) * mm, "end": v(-59.98, 45.37) * mm});
            skLineSegment(sketch, "E96.6", {"start": v(-60, 44.66) * mm, "end": v(-60, -44.66) * mm});
            skArc(sketch, "E97.0", {"start": v(-60, -44.66) * mm, "mid": v(-60, -45.02) * mm, "end": v(-59.98, -45.37) * mm});
            skArc(sketch, "E98.0", {"start": v(-59.98, 45.37) * mm, "mid": v(-60, 45.02) * mm, "end": v(-60, 44.66) * mm});
            skArc(sketch, "E99.0", {"start": v(60, 44.66) * mm, "mid": v(60, 45.02) * mm, "end": v(59.98, 45.37) * mm});
            skArc(sketch, "E100.0", {"start": v(59.98, -45.37) * mm, "mid": v(60, -45.02) * mm, "end": v(60, -44.66) * mm});
            skSolve(sketch);
        }
        {
            var Q0;
            {var subQ5=sQuery(id+"F16.wireOp",EDGE,"E79.0.0");Q0=makeQuery(id+"F16.imprint","IMPRINT",FACE,{"disambiguationData":[TD([[makeQuery(id+"F16.imprint","IMPRINT",EDGE,{"derivedFrom":subQ5}),1.0]])]});}
            var Q1;
            Q1=makeQuery(id+"F16.imprint","IMPRINT",FACE,{"disambiguationData":[TD([[makeQuery(id+"F16.imprint","IMPRINT",EDGE,{"derivedFrom":sQuery(id+"F16.wireOp",EDGE,"E81")}),-1.0]])]});
            var Q2;
            Q2=makeQuery(id+"F16.imprint","IMPRINT",FACE,{"disambiguationData":[TD([[makeQuery(id+"F16.imprint","IMPRINT",EDGE,{"derivedFrom":sQuery(id+"F16.wireOp",EDGE,"E88.MirrorC")}),1.0]])]});
            var Q3;
            Q3=makeQuery(id+"F2.opExtrude","CAP_FACE",FACE,{"disambiguationData":[OSD([sQuery(id+"F0.wireOp",EDGE,"E12"),sQuery(id+"F0.wireOp",EDGE,"E13"),sQuery(id+"F0.wireOp",EDGE,"E14"),sQuery(id+"F0.wireOp",EDGE,"E15"),sQuery(id+"F0.wireOp",EDGE,"E17.filletArc"),sQuery(id+"F0.wireOp",EDGE,"E18.filletArc"),sQuery(id+"F0.wireOp",EDGE,"E19.filletArc"),sQuery(id+"F0.wireOp",EDGE,"E20.filletArc"),sQuery(id+"F0.wireOp",EDGE,"E25.0"),sQuery(id+"F0.wireOp",EDGE,"E25.1"),sQuery(id+"F0.wireOp",EDGE,"E25.2"),sQuery(id+"F0.wireOp",EDGE,"E25.3"),sQuery(id+"F0.wireOp",EDGE,"E25.4"),sQuery(id+"F0.wireOp",EDGE,"E25.5"),sQuery(id+"F0.wireOp",EDGE,"E25.6"),sQuery(id+"F0.wireOp",EDGE,"E25.7")])],"isStart":false});
            extrude(context, id + "F17", {"entities" : qUnion([Q0, Q1, Q2]), "endBound" : BoundingType.UP_TO_SURFACE, "endBoundEntityFace" : qUnion([Q3]), "depth" : 25 * mm});
        }
    });
